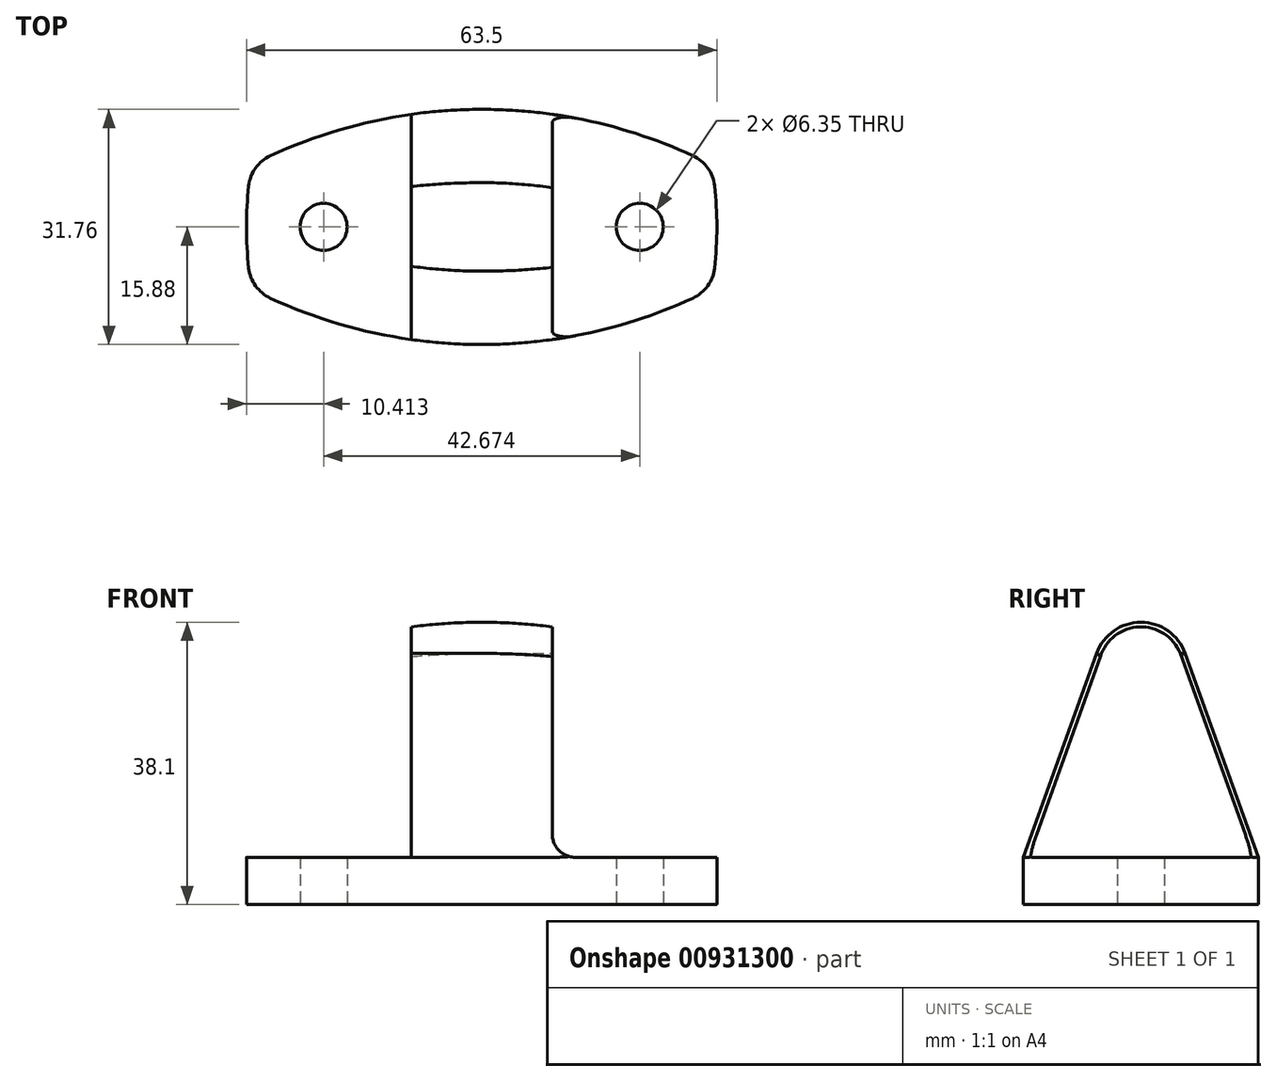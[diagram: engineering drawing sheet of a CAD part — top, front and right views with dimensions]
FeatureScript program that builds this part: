
annotation { "Feature Type Name" : "Feature", "Feature Type Description" : "" }
export const myFeature = defineFeature(function(context is Context, id is Id, definition is map)
    precondition{}
    {
        {
            var Q0;
            Q0=qCreatedBy(makeId("Top.planeOp"),FACE);
            var sketch = newSketch(context, id + "F0", { "sketchPlane" : qUnion([Q0])});
            skLineSegment(sketch, "E0", {"start": v(-31.75, 0) * mm, "end": v(31.75, 0) * mm, "construction": true});
            skLineSegment(sketch, "E1", {"start": v(0, 15.88) * mm, "end": v(0, -15.88) * mm, "construction": true});
            skArc(sketch, "E2", {"start": v(-31.04, 8.38) * mm, "mid": v(-31.75, 0) * mm, "end": v(-31.04, -8.38) * mm});
            skArc(sketch, "E3", {"start": v(31.04, -8.38) * mm, "mid": v(31.75, 0) * mm, "end": v(31.04, 8.38) * mm});
            skLineSegment(sketch, "E4", {"start": v(-31.04, 8.38) * mm, "end": v(31.04, 8.38) * mm, "construction": true});
            skLineSegment(sketch, "E5", {"start": v(-31.04, -8.38) * mm, "end": v(31.04, -8.38) * mm, "construction": true});
            skArc(sketch, "E6", {"start": v(31.04, 8.38) * mm, "mid": v(0, 15.88) * mm, "end": v(-31.04, 8.38) * mm});
            skArc(sketch, "E7", {"start": v(-31.04, -8.38) * mm, "mid": v(0, -15.88) * mm, "end": v(31.04, -8.38) * mm});
            skSolve(sketch);
        }
        {
            var Q0;
            Q0 = qSketchRegion(id + "F0", true);
            extrude(context, id + "F1", {"entities" : qUnion([Q0]), "depth" : 6.35 * mm, "offsetDistance" : 25.4 * mm});
        }
        {
            var Q0;
            Q0=makeQuery(id+"F1.opExtrude","SWEPT_EDGE",EDGE,{"disambiguationData":[OSD([sQuery(id+"F0.wireOp",EDGE,"E2"),sQuery(id+"F0.wireOp",EDGE,"E6")])]});
            var Q1;
            Q1=makeQuery(id+"F1.opExtrude","SWEPT_EDGE",EDGE,{"disambiguationData":[OSD([sQuery(id+"F0.wireOp",EDGE,"E3"),sQuery(id+"F0.wireOp",EDGE,"E6")])]});
            var Q2;
            Q2=makeQuery(id+"F1.opExtrude","SWEPT_EDGE",EDGE,{"disambiguationData":[OSD([sQuery(id+"F0.wireOp",EDGE,"E3"),sQuery(id+"F0.wireOp",EDGE,"E7")])]});
            var Q3;
            Q3=makeQuery(id+"F1.opExtrude","SWEPT_EDGE",EDGE,{"disambiguationData":[OSD([sQuery(id+"F0.wireOp",EDGE,"E2"),sQuery(id+"F0.wireOp",EDGE,"E7")])]});
            fillet(context, id + "F2", {"entities" : qUnion([Q0, Q1, Q2, Q3]), "radius" : 5.08 * mm, "tangentPropagation" : true, "allowEdgeOverflow" : false});
        }
        {
            var Q0;
            Q0=qCreatedBy(makeId("Right.planeOp"),FACE);
            var sketch = newSketch(context, id + "F3", { "sketchPlane" : qUnion([Q0])});
            skLineSegment(sketch, "E8", {"start": v(15.88, 6.35) * mm, "end": v(5.98, 33.9) * mm});
            skLineSegment(sketch, "E9", {"start": v(-5.98, 33.9) * mm, "end": v(-15.88, 6.35) * mm});
            skArc(sketch, "E10", {"start": v(5.98, 33.9) * mm, "mid": v(0, 38.1) * mm, "end": v(-5.98, 33.9) * mm});
            skLineSegment(sketch, "E11", {"start": v(15.88, 6.35) * mm, "end": v(-15.88, 6.35) * mm});
            skSolve(sketch);
        }
        {
            var Q0;
            Q0 = qSketchRegion(id + "F3", true);
            extrude(context, id + "F4", {"entities" : qUnion([Q0]), "operationType" : NewBodyOperationType.ADD, "endBound" : BoundingType.SYMMETRIC, "depth" : 19.05 * mm, "offsetDistance" : 25.4 * mm});
        }
        {
            var Q0;
            {var subQ0=sQuery(id+"F3.wireOp",EDGE,"E11");var subQ1=sQuery(id+"F3.wireOp",EDGE,"E8");var subQ2=sQuery(id+"F0.wireOp",EDGE,"E6");var subQ3=makeQuery(id+"F4.opExtrude","SWEPT_FACE",FACE,{"disambiguationData":[OSD([subQ0])]});Q0=makeQuery(id+"F4.boolean.opBoolean","SPLIT",FACE,{"disambiguationData":[TD([makeQuery(id+"F1.opExtrude","CAP_FACE",FACE,{"disambiguationData":[OSD([sQuery(id+"F0.wireOp",EDGE,"E2"),sQuery(id+"F0.wireOp",EDGE,"E3"),subQ2,sQuery(id+"F0.wireOp",EDGE,"E7")])],"isStart":false}),makeQuery(id+"F1.opExtrude","SWEPT_FACE",FACE,{"disambiguationData":[OSD([subQ2])]}),makeQuery(id+"F4.opExtrude","SWEPT_FACE",FACE,{"disambiguationData":[OSD([subQ1])]}),makeQuery(id+"F4.opExtrude","CAP_FACE",FACE,{"disambiguationData":[OSD([subQ1,sQuery(id+"F3.wireOp",EDGE,"E9"),sQuery(id+"F3.wireOp",EDGE,"E10"),subQ0])],"isStart":false}),subQ3])],"derivedFrom":subQ3});}
            var Q1;
            Q1=makeQuery(id+"F4.opExtrude","CAP_EDGE",EDGE,{"disambiguationData":[OSD([sQuery(id+"F3.wireOp",EDGE,"E8")])],"isStart":false});
            var Q2;
            Q2=makeQuery(id+"F4.opExtrude","CAP_EDGE",EDGE,{"disambiguationData":[OSD([sQuery(id+"F3.wireOp",EDGE,"E10")])],"isStart":false});
            var Q3;
            Q3=makeQuery(id+"F4.opExtrude","CAP_EDGE",EDGE,{"disambiguationData":[OSD([sQuery(id+"F3.wireOp",EDGE,"E9")])],"isStart":false});
            sweep(context, id + "F5", {"operationType" : NewBodyOperationType.REMOVE, "profiles" : qUnion([Q0]), "path" : qUnion([Q1, Q2, Q3])});
        }
        {
            var Q0;
            {var subQ0=sQuery(id+"F3.wireOp",EDGE,"E9");var subQ1=sQuery(id+"F0.wireOp",EDGE,"E7");var subQ2=sQuery(id+"F3.wireOp",EDGE,"E11");var subQ3=makeQuery(id+"F4.opExtrude","SWEPT_FACE",FACE,{"disambiguationData":[OSD([subQ2])]});Q0=makeQuery(id+"F4.boolean.opBoolean","SPLIT",FACE,{"disambiguationData":[TD([makeQuery(id+"F1.opExtrude","CAP_FACE",FACE,{"disambiguationData":[OSD([sQuery(id+"F0.wireOp",EDGE,"E2"),sQuery(id+"F0.wireOp",EDGE,"E3"),sQuery(id+"F0.wireOp",EDGE,"E6"),subQ1])],"isStart":false}),makeQuery(id+"F1.opExtrude","SWEPT_FACE",FACE,{"disambiguationData":[OSD([subQ1])]}),makeQuery(id+"F4.opExtrude","CAP_FACE",FACE,{"disambiguationData":[OSD([sQuery(id+"F3.wireOp",EDGE,"E8"),subQ0,sQuery(id+"F3.wireOp",EDGE,"E10"),subQ2])],"isStart":true}),makeQuery(id+"F4.opExtrude","SWEPT_FACE",FACE,{"disambiguationData":[OSD([subQ0])]}),subQ3])],"derivedFrom":subQ3});}
            var Q1;
            Q1=makeQuery(id+"F4.opExtrude","CAP_EDGE",EDGE,{"disambiguationData":[OSD([sQuery(id+"F3.wireOp",EDGE,"E9")])],"isStart":true});
            var Q2;
            Q2=makeQuery(id+"F4.opExtrude","CAP_EDGE",EDGE,{"disambiguationData":[OSD([sQuery(id+"F3.wireOp",EDGE,"E10")])],"isStart":true});
            var Q3;
            Q3=makeQuery(id+"F4.opExtrude","CAP_EDGE",EDGE,{"disambiguationData":[OSD([sQuery(id+"F3.wireOp",EDGE,"E8")])],"isStart":true});
            sweep(context, id + "F6", {"operationType" : NewBodyOperationType.REMOVE, "profiles" : qUnion([Q0]), "path" : qUnion([Q1, Q2, Q3])});
        }
        {
            var Q0;
            {var subQ0=sQuery(id+"F3.wireOp",EDGE,"E11");Q0=makeQuery(id+"F4.boolean.opBoolean","SPLIT",EDGE,{"disambiguationData":[topologyDisambiguationEdgeConnected([makeQuery(id+"F1.opExtrude","CAP_FACE",FACE,{"disambiguationData":[OSD([sQuery(id+"F0.wireOp",EDGE,"E2"),sQuery(id+"F0.wireOp",EDGE,"E3"),sQuery(id+"F0.wireOp",EDGE,"E6"),sQuery(id+"F0.wireOp",EDGE,"E7")])],"isStart":false}),makeQuery(id+"F4.opExtrude","CAP_FACE",FACE,{"disambiguationData":[OSD([sQuery(id+"F3.wireOp",EDGE,"E8"),sQuery(id+"F3.wireOp",EDGE,"E9"),sQuery(id+"F3.wireOp",EDGE,"E10"),subQ0])],"isStart":false})])],"derivedFrom":makeQuery(id+"F4.opExtrude","CAP_EDGE",EDGE,{"disambiguationData":[OSD([subQ0])],"isStart":false})});}
            var Q1;
            {var subQ0=sQuery(id+"F3.wireOp",EDGE,"E11");Q1=makeQuery(id+"F4.boolean.opBoolean","SPLIT",EDGE,{"disambiguationData":[topologyDisambiguationEdgeConnected([makeQuery(id+"F1.opExtrude","CAP_FACE",FACE,{"disambiguationData":[OSD([sQuery(id+"F0.wireOp",EDGE,"E2"),sQuery(id+"F0.wireOp",EDGE,"E3"),sQuery(id+"F0.wireOp",EDGE,"E6"),sQuery(id+"F0.wireOp",EDGE,"E7")])],"isStart":false}),makeQuery(id+"F4.opExtrude","CAP_FACE",FACE,{"disambiguationData":[OSD([sQuery(id+"F3.wireOp",EDGE,"E8"),sQuery(id+"F3.wireOp",EDGE,"E9"),sQuery(id+"F3.wireOp",EDGE,"E10"),subQ0])],"isStart":true})])],"derivedFrom":makeQuery(id+"F4.opExtrude","CAP_EDGE",EDGE,{"disambiguationData":[OSD([subQ0])],"isStart":true})});}
            fillet(context, id + "F7", {"entities" : qUnion([Q0, Q1]), "radius" : 3.17 * mm, "tangentPropagation" : true, "allowEdgeOverflow" : false});
        }
        {
            var Q0;
            Q0=makeQuery(id+"F1.opExtrude","CAP_FACE",FACE,{"disambiguationData":[OSD([sQuery(id+"F0.wireOp",EDGE,"E2"),sQuery(id+"F0.wireOp",EDGE,"E3"),sQuery(id+"F0.wireOp",EDGE,"E6"),sQuery(id+"F0.wireOp",EDGE,"E7")])],"isStart":true});
            var sketch = newSketch(context, id + "F8", { "sketchPlane" : qUnion([Q0])});
            skCircle(sketch, "E12", {"center": v(-21.34, 0) * mm, "radius": 3.18 * mm});
            skCircle(sketch, "E13", {"center": v(21.34, 0) * mm, "radius": 3.18 * mm});
            skLineSegment(sketch, "E14", {"start": v(-21.34, 0) * mm, "end": v(21.34, 0) * mm});
            skSolve(sketch);
        }
        {
            var Q0;
            Q0 = qSketchRegion(id + "F8", true);
            extrude(context, id + "F9", {"entities" : qUnion([Q0]), "operationType" : NewBodyOperationType.REMOVE, "endBound" : BoundingType.THROUGH_ALL, "oppositeDirection" : true, "depth" : 25.4 * mm, "offsetDistance" : 25.4 * mm});
        }
    });
